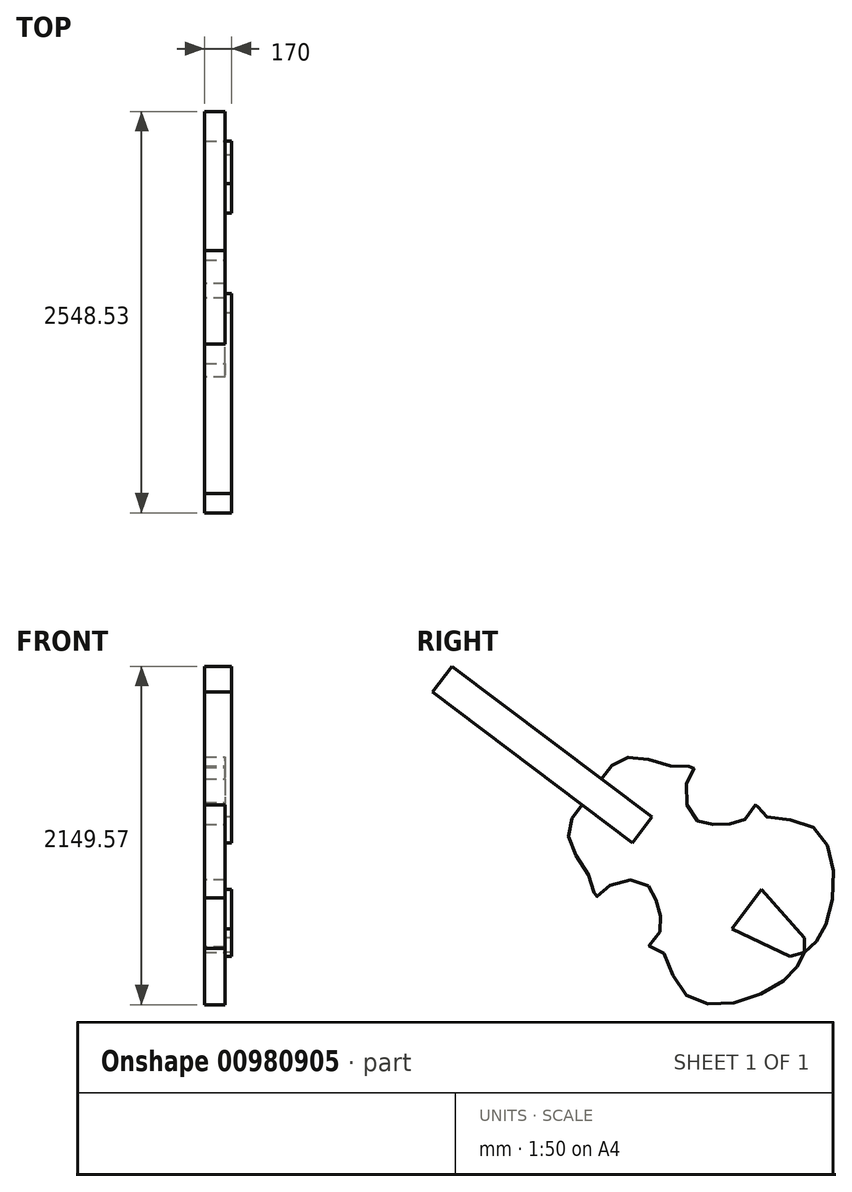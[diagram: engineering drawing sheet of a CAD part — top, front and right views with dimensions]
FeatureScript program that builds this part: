
annotation { "Feature Type Name" : "Feature", "Feature Type Description" : "" }
export const myFeature = defineFeature(function(context is Context, id is Id, definition is map)
    precondition{}
    {
        {
            var Q0;
            Q0=qCreatedBy(makeId("Right.planeOp"),FACE);
            cPlane(context, id + "F0", {"entities" : qUnion([Q0]), "cplaneType" : CPlaneType.OFFSET, "offset" : 813 * mm, "width" : 150 * mm, "height" : 150 * mm});
        }
        {
            var Q0;
            Q0=qCreatedBy(id+"F0.planeOp",FACE);
            var sketch = newSketch(context, id + "F1", { "sketchPlane" : qUnion([Q0])});
            skFitSpline(sketch, "E0", {"points": [v(698.8, -385.5) * mm, v(577.05, -501.05) * mm, v(539.1, -688.88) * mm, v(682.04, -947.96) * mm, v(701.04, -1043.77) * mm, v(802.05, -960.42) * mm, v(1034.84, -962.55) * mm, v(1102.54, -1108.14) * mm, v(1111.35, -1263.48) * mm, v(1032.3, -1364.88) * mm, v(1100.94, -1359.6) * mm, v(1238.98, -1618.72) * mm, v(1554.5, -1716) * mm, v(1933.01, -1540.6) * mm, v(2030.18, -1390.64) * mm], "startDerivative": vector(-1971.96, -1478.15) * mm, "endDerivative": vector(1061.36, 2316.29) * mm});
            skLineSegment(sketch, "E1", {"start": v(698.8, -385.5) * mm, "end": v(2030.18, -1390.64) * mm});
            skFitSpline(sketch, "E2.MirrorCS", {"points": [v(698.8, -385.5) * mm, v(776.6, -236.74) * mm, v(946.85, -148.8) * mm, v(1235.18, -215.31) * mm, v(1332.52, -207.34) * mm, v(1280.03, -327.31) * mm, v(1345.84, -550.63) * mm, v(1504.4, -575.86) * mm, v(1656.21, -541.79) * mm, v(1732.08, -437.97) * mm, v(1745.8, -505.45) * mm, v(2032.83, -567.24) * mm, v(2212.8, -844.04) * mm, v(2147.78, -1256.12) * mm, v(2030.18, -1390.64) * mm], "startDerivative": vector(881.51, 2301.4) * mm, "endDerivative": vector(-1937, -1655.2) * mm});
            skLineSegment(sketch, "E3", {"start": v(-330.79, 263.27) * mm, "end": v(937.6, -694.33) * mm});
            skLineSegment(sketch, "E4", {"start": v(937.6, -694.33) * mm, "end": v(999.42, -612.45) * mm});
            skLineSegment(sketch, "E5.MirrorCS", {"start": v(-207.15, 427.04) * mm, "end": v(1061.24, -530.57) * mm});
            skLineSegment(sketch, "E6.MirrorCS", {"start": v(1061.24, -530.57) * mm, "end": v(999.42, -612.45) * mm});
            skLineSegment(sketch, "E7", {"start": v(-330.79, 263.27) * mm, "end": v(-207.15, 427.04) * mm});
            skPoint(sketch, "E8.endSnap0", {"position": v(1364.5, -888.07) * mm});
            skLineSegment(sketch, "E9", {"start": v(1571.46, -1239.64) * mm, "end": v(1939.65, -1415.49) * mm});
            skLineSegment(sketch, "E10", {"start": v(1939.65, -1415.49) * mm, "end": v(2030.18, -1390.64) * mm});
            skLineSegment(sketch, "E11", {"start": v(1571.46, -1239.64) * mm, "end": v(1665.38, -1115.23) * mm});
            skLineSegment(sketch, "E12.MirrorCS", {"start": v(1759.3, -990.82) * mm, "end": v(2029.28, -1296.77) * mm});
            skLineSegment(sketch, "E13.MirrorCS", {"start": v(1759.3, -990.82) * mm, "end": v(1665.38, -1115.23) * mm});
            skLineSegment(sketch, "E14.MirrorCS", {"start": v(2029.28, -1296.77) * mm, "end": v(2030.18, -1390.64) * mm});
            skSolve(sketch);
        }
        {
            var Q0;
            Q0 = qSketchRegion(id + "F1", true);
            extrude(context, id + "F2", {"entities" : qUnion([Q0]), "oppositeDirection" : true, "depth" : 130 * mm, "offsetDistance" : 25 * mm});
        }
        {
            var Q0;
            Q0=makeQuery(id+"F1.imprint","IMPRINT",FACE,{"disambiguationData":[TD([[makeQuery(id+"F1.imprint","IMPRINT",EDGE,{"derivedFrom":sQuery(id+"F1.wireOp",EDGE,"E12.MirrorCS")}),-1.0]])]});
            var Q1;
            Q1=makeQuery(id+"F1.imprint","IMPRINT",FACE,{"disambiguationData":[TD([[makeQuery(id+"F1.imprint","IMPRINT",EDGE,{"derivedFrom":sQuery(id+"F1.wireOp",EDGE,"E9")}),1.0]])]});
            var Q2;
            {var subQ0=sQuery(id+"F1.wireOp",EDGE,"E7");Q2=makeQuery(id+"F1.imprint","IMPRINT",FACE,{"disambiguationData":[TD([[makeQuery(id+"F1.imprint","IMPRINT",EDGE,{"derivedFrom":subQ0}),-1.0]])]});}
            var Q3;
            {var subQ3=sQuery(id+"F1.wireOp",EDGE,"E6.MirrorCS");Q3=makeQuery(id+"F1.imprint","IMPRINT",FACE,{"disambiguationData":[TD([[makeQuery(id+"F1.imprint","IMPRINT",EDGE,{"derivedFrom":subQ3}),-1.0]])]});}
            var Q4;
            {var subQ5=sQuery(id+"F1.wireOp",EDGE,"E4");Q4=makeQuery(id+"F1.imprint","IMPRINT",FACE,{"disambiguationData":[TD([[makeQuery(id+"F1.imprint","IMPRINT",EDGE,{"derivedFrom":subQ5}),1.0]])]});}
            extrude(context, id + "F3", {"entities" : qUnion([Q0, Q1, Q2, Q3, Q4]), "operationType" : NewBodyOperationType.ADD, "depth" : 40 * mm, "offsetDistance" : 25 * mm});
        }
    });
